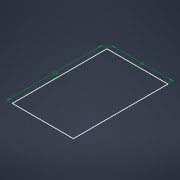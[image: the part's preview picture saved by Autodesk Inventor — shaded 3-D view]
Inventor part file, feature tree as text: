
AUTODESK INVENTOR PART (.ipt)
format: ipt  version: 2022 (Build 260153070, 153G)  size: 88,064 bytes
history: native  units: mm
features: other x1, extrude x1, sketch x1
ambient origin geometry x8: Origin, YZ Plane, XZ Plane, XY Plane, X Axis, Y Axis, Z Axis, Center Point
bodies: Body1 (feature_tree)
feature tree (3):
  other  "Твердое тело1"
  extrude  "Выдавливание1"  Depth=82.0mm
  sketch  "Эскиз1"
